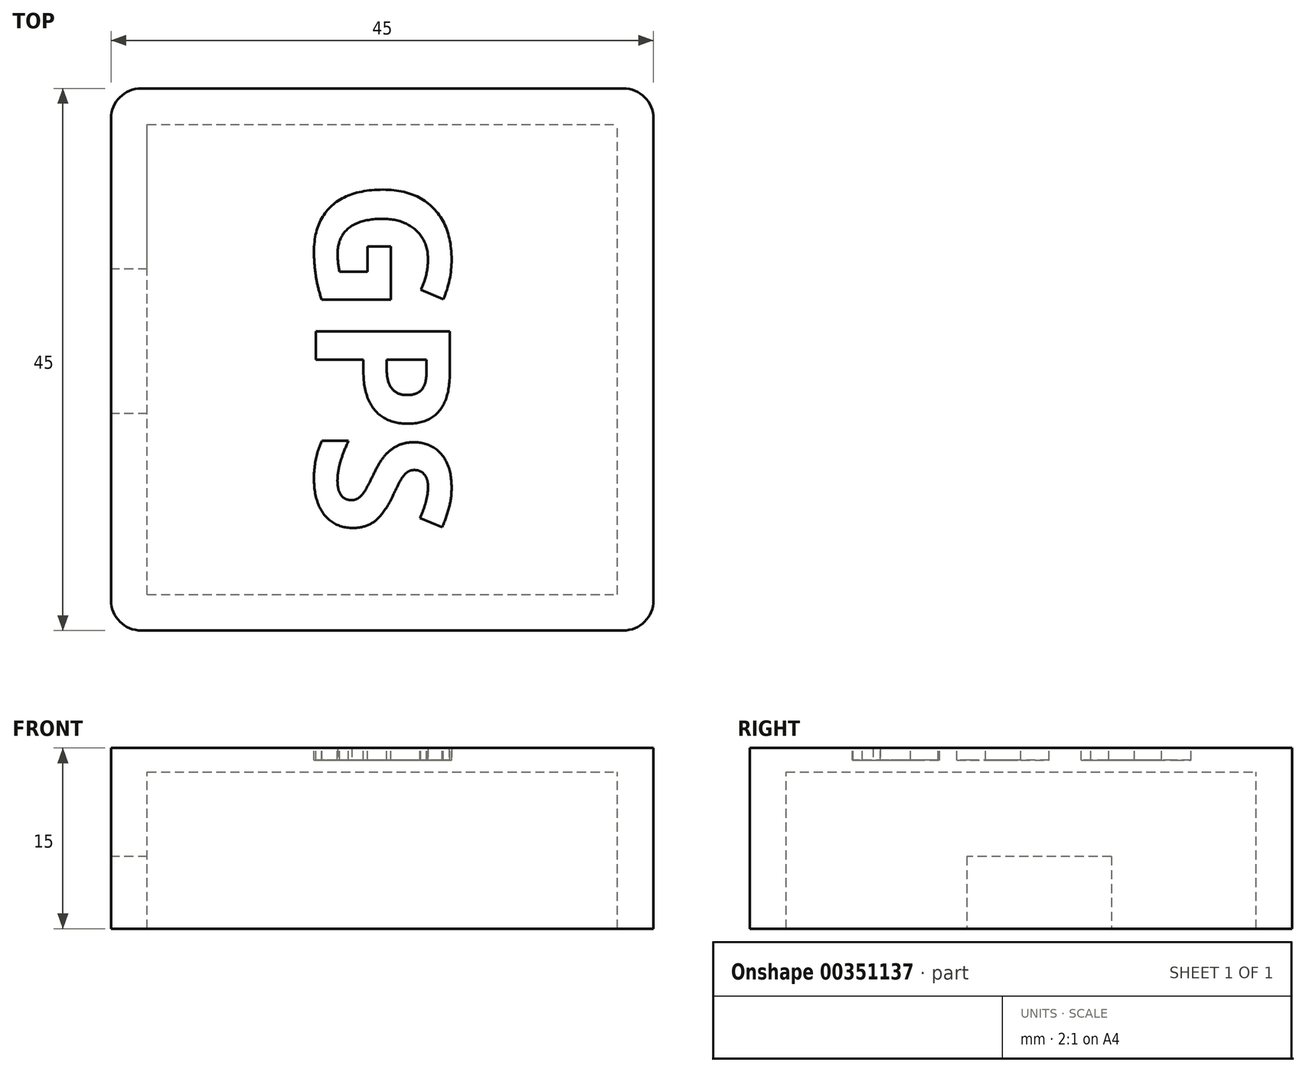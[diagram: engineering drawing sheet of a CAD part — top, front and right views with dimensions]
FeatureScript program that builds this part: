
annotation { "Feature Type Name" : "Feature", "Feature Type Description" : "" }
export const myFeature = defineFeature(function(context is Context, id is Id, definition is map)
    precondition{}
    {
        {
            var Q0;
            Q0=qCreatedBy(makeId("Top.planeOp"),FACE);
            var sketch = newSketch(context, id + "F0", { "sketchPlane" : qUnion([Q0])});
            skLineSegment(sketch, "E0.bottom", {"start": v(-20, 22.5) * mm, "end": v(20, 22.5) * mm});
            skLineSegment(sketch, "E0.top", {"start": v(-20, -22.5) * mm, "end": v(20, -22.5) * mm});
            skLineSegment(sketch, "E0.left", {"start": v(-22.5, 20) * mm, "end": v(-22.5, 10) * mm});
            skLineSegment(sketch, "E0.right", {"start": v(22.5, 20) * mm, "end": v(22.5, -20) * mm});
            skPoint(sketch, "E1.visualSharp", {"position": v(-22.5, 22.5) * mm});
            skArc(sketch, "E1.filletArc", {"start": v(-20, 22.5) * mm, "mid": v(-21.77, 21.77) * mm, "end": v(-22.5, 20) * mm});
            skPoint(sketch, "E2.visualSharp", {"position": v(22.5, 22.5) * mm});
            skArc(sketch, "E2.filletArc", {"start": v(22.5, 20) * mm, "mid": v(21.77, 21.77) * mm, "end": v(20, 22.5) * mm});
            skPoint(sketch, "E3.visualSharp", {"position": v(22.5, -22.5) * mm});
            skArc(sketch, "E3.filletArc", {"start": v(20, -22.5) * mm, "mid": v(21.77, -21.77) * mm, "end": v(22.5, -20) * mm});
            skPoint(sketch, "E4.visualSharp", {"position": v(-22.5, -22.5) * mm});
            skArc(sketch, "E4.filletArc", {"start": v(-22.5, -20) * mm, "mid": v(-21.77, -21.77) * mm, "end": v(-20, -22.5) * mm});
            skLineSegment(sketch, "E5.trimOffspring", {"start": v(-22.5, -10) * mm, "end": v(-22.5, -20) * mm});
            skLineSegment(sketch, "E6", {"start": v(-22.5, 10) * mm, "end": v(-22.5, -10) * mm});
            skSolve(sketch);
        }
        {
            var Q0;
            Q0 = qSketchRegion(id + "F0", true);
            extrude(context, id + "F1", {"entities" : qUnion([Q0]), "depth" : 2 * mm, "offsetDistance" : 25 * mm});
        }
        {
            var Q0;
            Q0=makeQuery(id+"F1.opExtrude","CAP_FACE",FACE,{"disambiguationData":[OSD([sQuery(id+"F0.wireOp",EDGE,"E0.bottom"),sQuery(id+"F0.wireOp",EDGE,"E0.top"),sQuery(id+"F0.wireOp",EDGE,"E0.left"),sQuery(id+"F0.wireOp",EDGE,"E0.right"),sQuery(id+"F0.wireOp",EDGE,"E1.filletArc"),sQuery(id+"F0.wireOp",EDGE,"E2.filletArc"),sQuery(id+"F0.wireOp",EDGE,"E3.filletArc"),sQuery(id+"F0.wireOp",EDGE,"E4.filletArc"),sQuery(id+"F0.wireOp",EDGE,"J8sy2c8t-h1tT-nzvo-lcWc-7fI8XEbyrLXh"),sQuery(id+"F0.wireOp",EDGE,"2URSMe59-cWbT-6hSF-MUZl-X1Aq8mDiMcGA"),sQuery(id+"F0.wireOp",EDGE,"WA30e765-MKc8-Sa3M-G6Ij-aCtr58VPHBoj"),sQuery(id+"F0.wireOp",EDGE,"E5.trimOffspring")])],"isStart":false});
            var sketch = newSketch(context, id + "F2", { "sketchPlane" : qUnion([Q0])});
            skText(sketch, "E7", { "text": "GPS", "fontName": "OpenSans-Bold.ttf"});
            const initialGuessF2  = {"E7": [-0.00551, 0.015, 0, -1, 0.0112]};
            skSetInitialGuess(sketch, initialGuessF2);
            skSolve(sketch);
        }
        {
            var Q0;
            Q0 = qSketchRegion(id + "F2", true);
            extrude(context, id + "F3", {"entities" : qUnion([Q0]), "operationType" : NewBodyOperationType.REMOVE, "oppositeDirection" : true, "depth" : 1 * mm, "offsetDistance" : 25 * mm});
        }
        {
            var Q0;
            Q0=makeQuery(id+"F1.opExtrude","CAP_FACE",FACE,{"disambiguationData":[OSD([sQuery(id+"F0.wireOp",EDGE,"E0.bottom"),sQuery(id+"F0.wireOp",EDGE,"E0.top"),sQuery(id+"F0.wireOp",EDGE,"E0.left"),sQuery(id+"F0.wireOp",EDGE,"E0.right"),sQuery(id+"F0.wireOp",EDGE,"E1.filletArc"),sQuery(id+"F0.wireOp",EDGE,"E2.filletArc"),sQuery(id+"F0.wireOp",EDGE,"E3.filletArc"),sQuery(id+"F0.wireOp",EDGE,"E4.filletArc"),sQuery(id+"F0.wireOp",EDGE,"J8sy2c8t-h1tT-nzvo-lcWc-7fI8XEbyrLXh"),sQuery(id+"F0.wireOp",EDGE,"2URSMe59-cWbT-6hSF-MUZl-X1Aq8mDiMcGA"),sQuery(id+"F0.wireOp",EDGE,"WA30e765-MKc8-Sa3M-G6Ij-aCtr58VPHBoj"),sQuery(id+"F0.wireOp",EDGE,"E5.trimOffspring")])],"isStart":true});
            var sketch = newSketch(context, id + "F4", { "sketchPlane" : qUnion([Q0])});
            skLineSegment(sketch, "E8.bottom", {"start": v(-19.5, 19.5) * mm, "end": v(19.5, 19.5) * mm});
            skLineSegment(sketch, "E8.top", {"start": v(-19.5, -19.5) * mm, "end": v(19.5, -19.5) * mm});
            skLineSegment(sketch, "E8.left", {"start": v(-19.5, 20) * mm, "end": v(-19.5, 19.5) * mm});
            skLineSegment(sketch, "E8.right", {"start": v(19.5, 19.5) * mm, "end": v(19.5, -19.5) * mm});
            skLineSegment(sketch, "E9", {"start": v(-22.5, 20) * mm, "end": v(-22.5, 20) * mm});
            skLineSegment(sketch, "E10", {"start": v(-20, 22.5) * mm, "end": v(20, 22.5) * mm});
            skLineSegment(sketch, "E11", {"start": v(22.5, 20) * mm, "end": v(22.5, -20) * mm});
            skLineSegment(sketch, "E12", {"start": v(20, -22.5) * mm, "end": v(-20, -22.5) * mm});
            skLineSegment(sketch, "E13", {"start": v(-22.5, -20) * mm, "end": v(-22.5, -20) * mm});
            skLineSegment(sketch, "E14.trimOffspring", {"start": v(-19.5, -19.5) * mm, "end": v(-19.5, -20) * mm});
            skArc(sketch, "E15", {"start": v(-20, 22.5) * mm, "mid": v(-21.77, 21.77) * mm, "end": v(-22.5, 20) * mm});
            skArc(sketch, "E16", {"start": v(22.5, 20) * mm, "mid": v(21.77, 21.77) * mm, "end": v(20, 22.5) * mm});
            skArc(sketch, "E17", {"start": v(20, -22.5) * mm, "mid": v(21.77, -21.77) * mm, "end": v(22.5, -20) * mm});
            skArc(sketch, "E18", {"start": v(-22.5, -20) * mm, "mid": v(-21.77, -21.77) * mm, "end": v(-20, -22.5) * mm});
            skLineSegment(sketch, "E19", {"start": v(-19.5, 19.5) * mm, "end": v(-19.5, -19.5) * mm});
            skLineSegment(sketch, "E20", {"start": v(-22.5, 20) * mm, "end": v(-22.5, -20) * mm});
            skSolve(sketch);
        }
        {
            var Q0;
            Q0 = qSketchRegion(id + "F4", true);
            extrude(context, id + "F5", {"entities" : qUnion([Q0]), "operationType" : NewBodyOperationType.ADD, "depth" : 13 * mm});
        }
        {
            var Q0;
            Q0=makeQuery(id+"F5.boolean.opBoolean","MERGE",FACE,{"derivedFrom":[makeQuery(id+"F1.opExtrude","SWEPT_FACE",FACE,{"disambiguationData":[OSD([sQuery(id+"F0.wireOp",EDGE,"E0.left"),sQuery(id+"F0.wireOp",EDGE,"E5.trimOffspring"),sQuery(id+"F0.wireOp",EDGE,"E6")])]}),makeQuery(id+"F5.opExtrude","SWEPT_FACE",FACE,{"disambiguationData":[OSD([sQuery(id+"F4.wireOp",EDGE,"E20")])]})]});
            var sketch = newSketch(context, id + "F6", { "sketchPlane" : qUnion([Q0])});
            skLineSegment(sketch, "E21.bottom", {"start": v(-7.5, -7) * mm, "end": v(4.5, -7) * mm});
            skLineSegment(sketch, "E21.top", {"start": v(-7.5, -13) * mm, "end": v(4.5, -13) * mm});
            skLineSegment(sketch, "E21.left", {"start": v(-7.5, -7) * mm, "end": v(-7.5, -13) * mm});
            skLineSegment(sketch, "E21.right", {"start": v(4.5, -7) * mm, "end": v(4.5, -13) * mm});
            skSolve(sketch);
        }
        {
            var Q0;
            Q0 = qSketchRegion(id + "F6", true);
            extrude(context, id + "F7", {"entities" : qUnion([Q0]), "operationType" : NewBodyOperationType.REMOVE, "oppositeDirection" : true, "depth" : 5 * mm});
        }
    });
